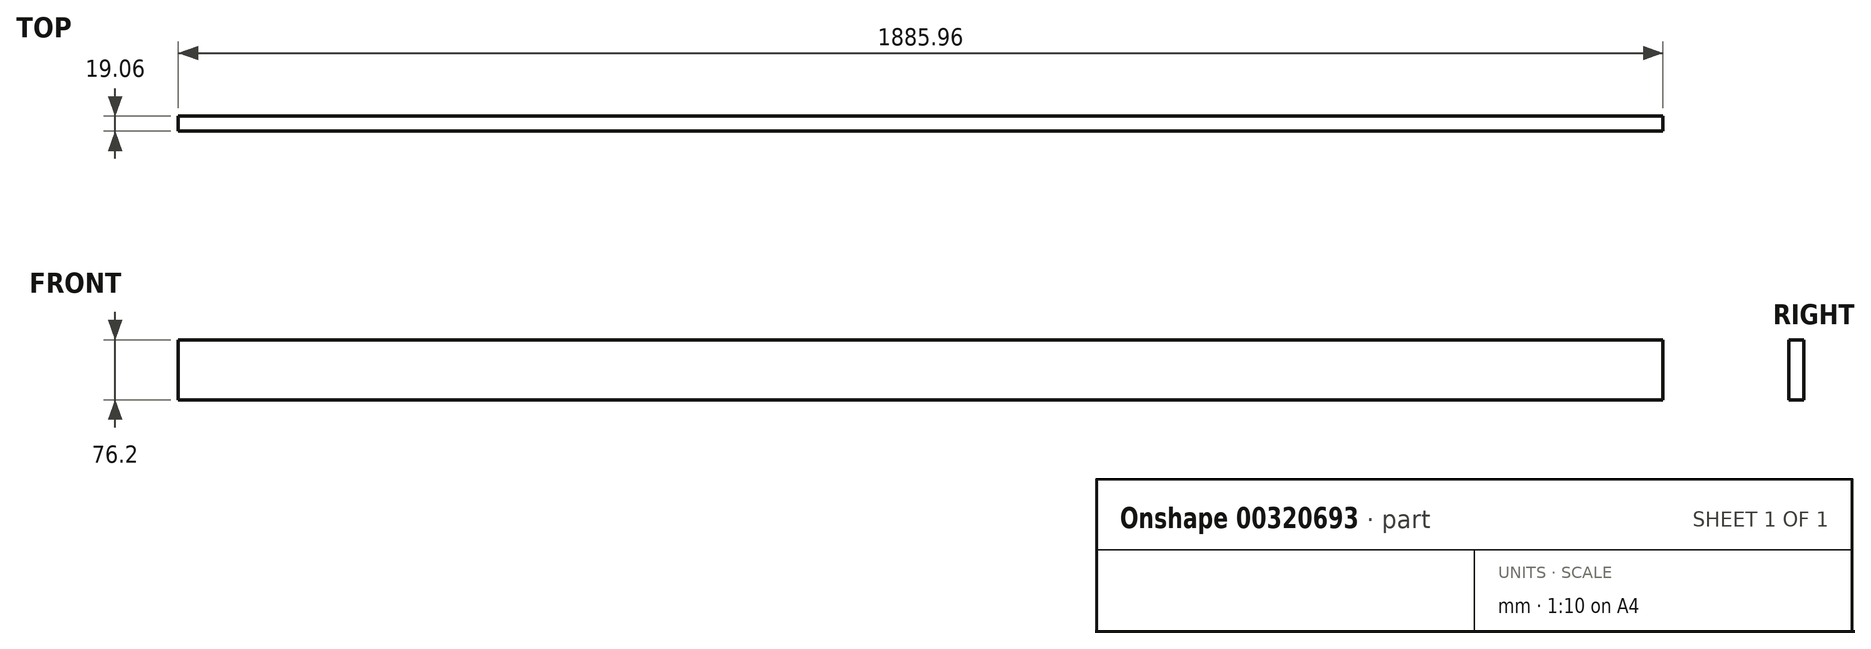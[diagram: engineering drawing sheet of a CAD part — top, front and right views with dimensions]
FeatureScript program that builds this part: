
annotation { "Feature Type Name" : "Feature", "Feature Type Description" : "" }
export const myFeature = defineFeature(function(context is Context, id is Id, definition is map)
    precondition{}
    {
        {
            var Q0;
            Q0=qCreatedBy(makeId("Front.planeOp"),FACE);
            var sketch = newSketch(context, id + "F0", { "sketchPlane" : qUnion([Q0])});
            skLineSegment(sketch, "E0.bottom", {"start": v(-942.98, -38.1) * mm, "end": v(942.97, -38.1) * mm});
            skLineSegment(sketch, "E0.top", {"start": v(-942.98, 38.1) * mm, "end": v(942.97, 38.1) * mm});
            skLineSegment(sketch, "E0.left", {"start": v(-942.98, -38.1) * mm, "end": v(-942.98, 38.1) * mm});
            skLineSegment(sketch, "E0.right", {"start": v(942.97, -38.1) * mm, "end": v(942.97, 38.1) * mm});
            skPoint(sketch, "E0.middle", {"position": v(0, 0) * mm});
            skSolve(sketch);
        }
        {
            var Q0;
            Q0 = qSketchRegion(id + "F0", true);
            extrude(context, id + "F1", {"entities" : qUnion([Q0]), "depth" : 19.05 * mm, "symmetric" : true});
        }
    });
